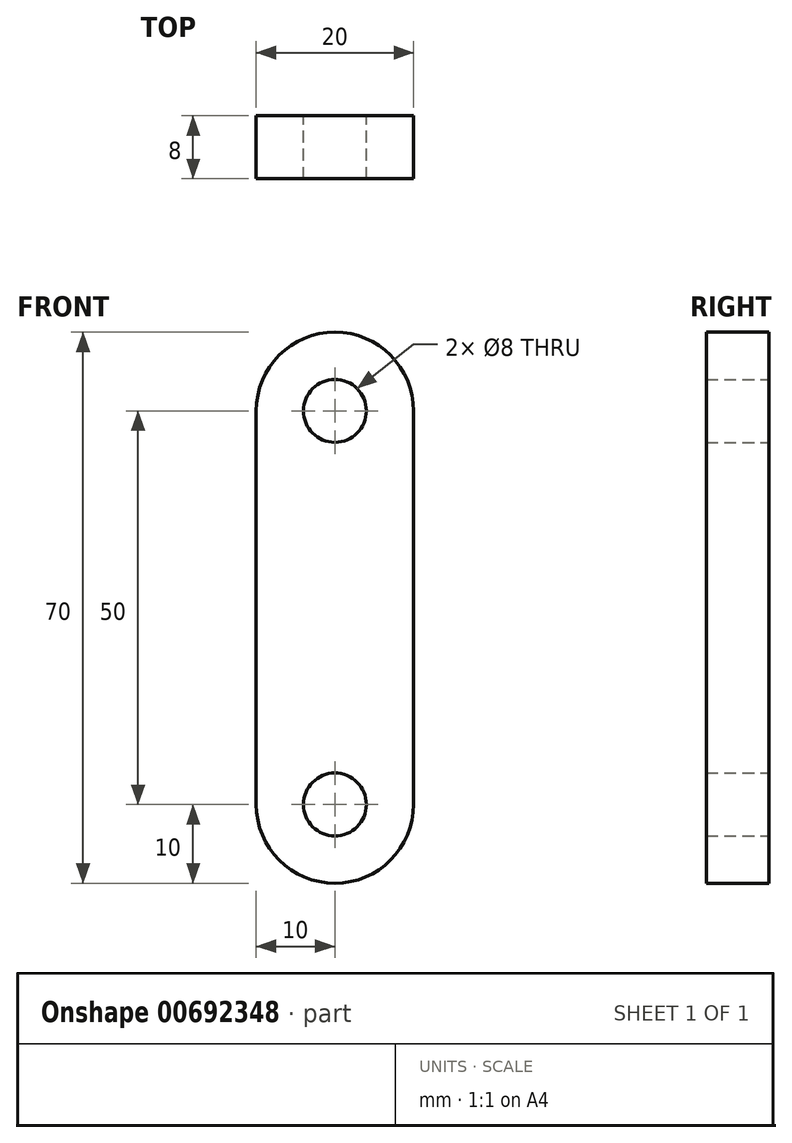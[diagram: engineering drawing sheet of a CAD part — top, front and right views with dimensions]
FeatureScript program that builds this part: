
annotation { "Feature Type Name" : "Feature", "Feature Type Description" : "" }
export const myFeature = defineFeature(function(context is Context, id is Id, definition is map)
    precondition{}
    {
        {
            var Q0;
            Q0=qCreatedBy(makeId("Front.planeOp"),FACE);
            var sketch = newSketch(context, id + "F0", { "sketchPlane" : qUnion([Q0])});
            skCircle(sketch, "E0", {"center": v(0, 0) * mm, "radius": 4 * mm});
            skArc(sketch, "E1", {"start": v(-10, 0) * mm, "mid": v(0, -10) * mm, "end": v(10, 0) * mm});
            skLineSegment(sketch, "E2", {"start": v(-10, 0) * mm, "end": v(-10, 50) * mm});
            skLineSegment(sketch, "E3", {"start": v(10, 50) * mm, "end": v(10, 0) * mm});
            skCircle(sketch, "E4", {"center": v(0, 50) * mm, "radius": 4 * mm});
            skArc(sketch, "E5", {"start": v(10, 50) * mm, "mid": v(0, 60) * mm, "end": v(-10, 50) * mm});
            skSolve(sketch);
        }
        {
            var Q0;
            Q0 = qSketchRegion(id + "F0", true);
            extrude(context, id + "F1", {"entities" : qUnion([Q0]), "depth" : 8 * mm, "offsetDistance" : 25 * mm});
        }
    });
